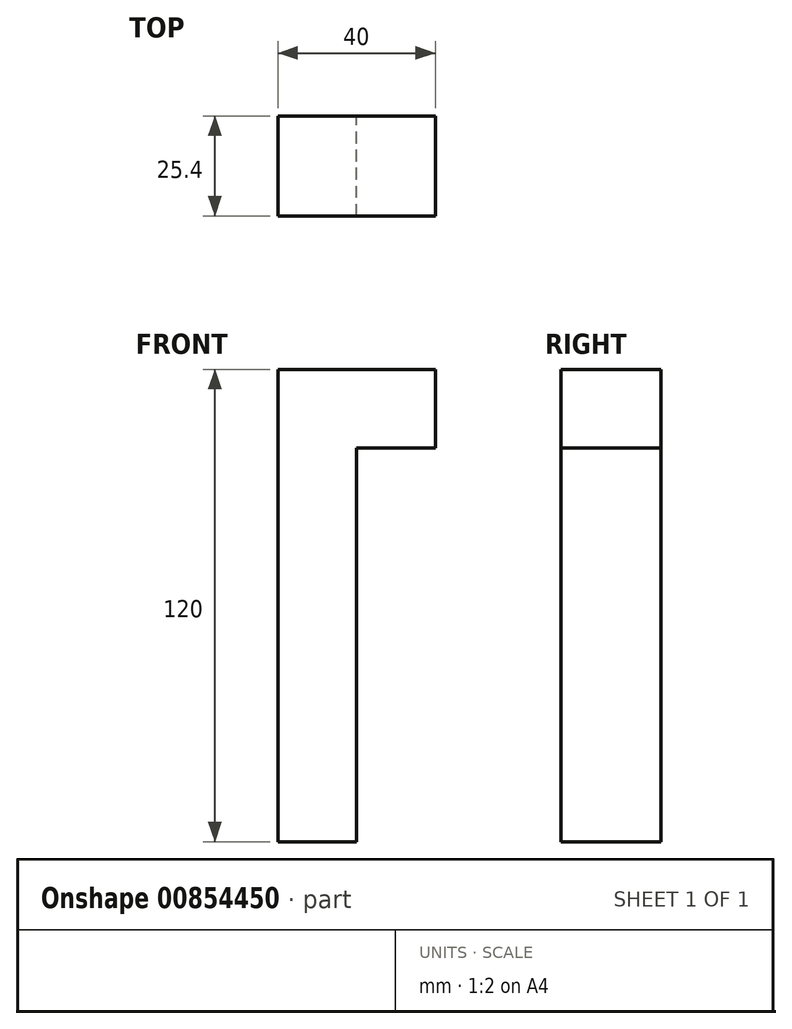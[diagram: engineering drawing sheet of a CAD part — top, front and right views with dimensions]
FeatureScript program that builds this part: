
annotation { "Feature Type Name" : "Feature", "Feature Type Description" : "" }
export const myFeature = defineFeature(function(context is Context, id is Id, definition is map)
    precondition{}
    {
        {
            var Q0;
            Q0=qCreatedBy(makeId("Front.planeOp"),FACE);
            var sketch = newSketch(context, id + "F0", { "sketchPlane" : qUnion([Q0])});
            skLineSegment(sketch, "E0.bottom", {"start": v(-10, 50) * mm, "end": v(10, 50) * mm});
            skLineSegment(sketch, "E0.top", {"start": v(-10, -50) * mm, "end": v(10, -50) * mm});
            skLineSegment(sketch, "E0.left", {"start": v(-10, 50) * mm, "end": v(-10, -50) * mm});
            skLineSegment(sketch, "E0.right", {"start": v(10, 50) * mm, "end": v(10, -50) * mm});
            skPoint(sketch, "E0.middle", {"position": v(0, 0) * mm});
            skLineSegment(sketch, "E1.bottom", {"start": v(-10, 50) * mm, "end": v(30, 50) * mm});
            skLineSegment(sketch, "E1.top", {"start": v(-10, 70) * mm, "end": v(30, 70) * mm});
            skLineSegment(sketch, "E1.left", {"start": v(-10, 70) * mm, "end": v(-10, 50) * mm});
            skLineSegment(sketch, "E1.right", {"start": v(30, 70) * mm, "end": v(30, 50) * mm});
            skSolve(sketch);
        }
        {
            var Q0;
            Q0 = qSketchRegion(id + "F0", true);
            extrude(context, id + "F1", {"entities" : qUnion([Q0]), "depth" : 25.4 * mm, "offsetDistance" : 25.4 * mm});
        }
    });
